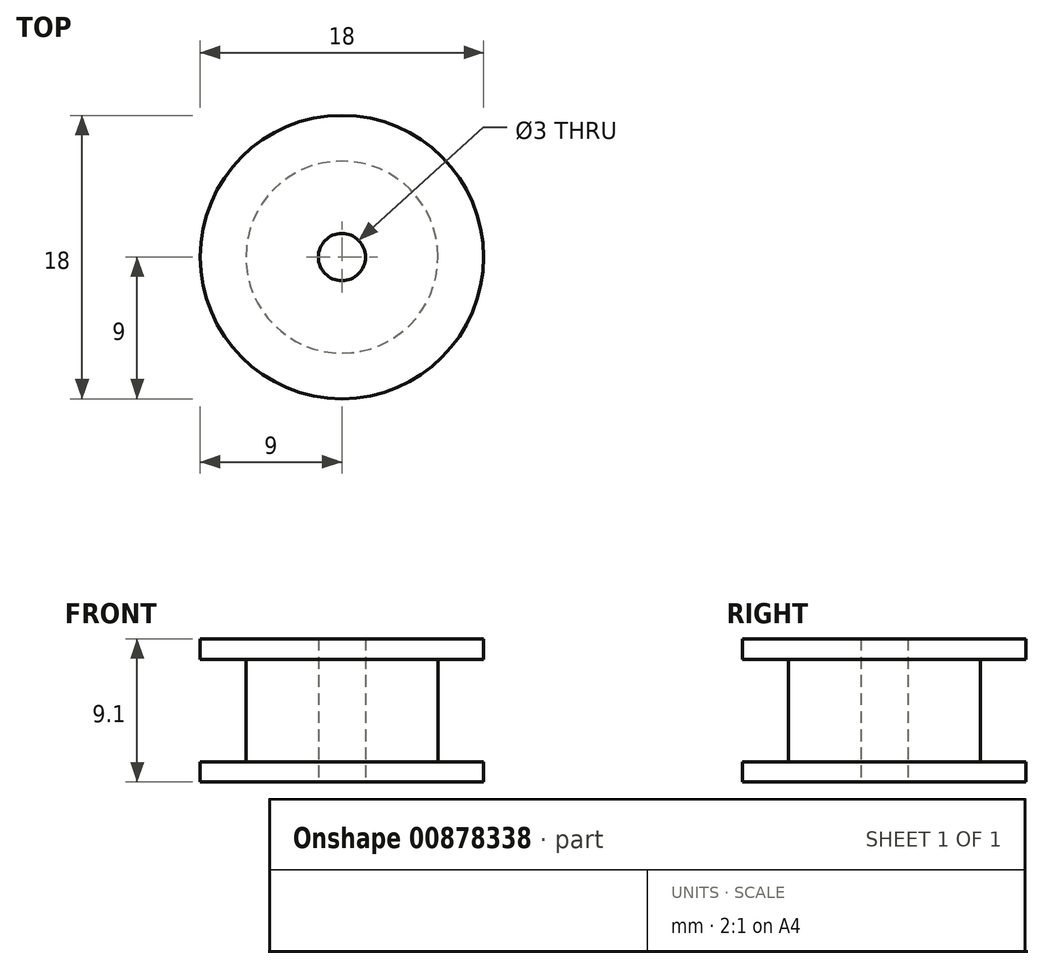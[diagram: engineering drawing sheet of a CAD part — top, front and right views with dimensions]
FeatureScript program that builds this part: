
annotation { "Feature Type Name" : "Feature", "Feature Type Description" : "" }
export const myFeature = defineFeature(function(context is Context, id is Id, definition is map)
    precondition{}
    {
        {
            var Q0;
            Q0=qCreatedBy(makeId("Top.planeOp"),FACE);
            var sketch = newSketch(context, id + "F0", { "sketchPlane" : qUnion([Q0])});
            skCircle(sketch, "E0", {"center": v(0, 0) * mm, "radius": 9 * mm});
            skCircle(sketch, "E1", {"center": v(0, 0) * mm, "radius": 1.5 * mm});
            skSolve(sketch);
        }
        {
            var Q0;
            Q0=qSketchRegion(id+"F0",true);
            extrude(context, id + "F1", {"entities" : qUnion([Q0]), "depth" : 1.3 * mm, "offsetDistance" : 25 * mm});
        }
        {
            var Q0;
            Q0=makeQuery(id+"F1.opExtrude","CAP_FACE",FACE,{"disambiguationData":[OSD([sQuery(id+"F0.wireOp",EDGE,"E0"),sQuery(id+"F0.wireOp",EDGE,"E1")])],"isStart":false});
            var sketch = newSketch(context, id + "F2", { "sketchPlane" : qUnion([Q0])});
            skCircle(sketch, "E2", {"center": v(0, 0) * mm, "radius": 6.1 * mm});
            skCircle(sketch, "E3.0", {"center": v(0, 0) * mm, "radius": 1.5 * mm});
            skSolve(sketch);
        }
        {
            var Q0;
            Q0=qSketchRegion(id+"F2",true);
            extrude(context, id + "F3", {"entities" : qUnion([Q0]), "operationType" : NewBodyOperationType.ADD, "depth" : 6.5 * mm, "offsetDistance" : 25 * mm});
        }
        {
            var Q0;
            Q0=makeQuery(id+"F3.opExtrude","CAP_FACE",FACE,{"disambiguationData":[OSD([sQuery(id+"F2.wireOp",EDGE,"E2"),sQuery(id+"F2.wireOp",EDGE,"E3.0")])],"isStart":false});
            var sketch = newSketch(context, id + "F4", { "sketchPlane" : qUnion([Q0])});
            skCircle(sketch, "E4", {"center": v(0, 0) * mm, "radius": 9 * mm});
            skCircle(sketch, "E5.0", {"center": v(0, 0) * mm, "radius": 1.5 * mm});
            skSolve(sketch);
        }
        {
            var Q0;
            Q0=makeQuery(id+"F4.imprint","IMPRINT",FACE,{"disambiguationData":[TD([[makeQuery(id+"F4.imprint","IMPRINT",EDGE,{"derivedFrom":sQuery(id+"F4.wireOp",EDGE,"E5.0")}),-1.0]])]});
            var Q1;
            Q1=makeQuery(id+"F4.imprint","IMPRINT",FACE,{"disambiguationData":[TD([[makeQuery(id+"F4.imprint","IMPRINT",EDGE,{"derivedFrom":sQuery(id+"F4.wireOp",EDGE,"E4")}),1.0]])]});
            extrude(context, id + "F5", {"entities" : qUnion([Q0, Q1]), "operationType" : NewBodyOperationType.ADD, "depth" : 1.3 * mm, "offsetDistance" : 25 * mm});
        }
    });
